# Revit family: AKTSCP38
name_source: partatom
category: Lighting Fixtures
revit_build: Autodesk Revit 2014 (Build: 20130308_1515(x64)
units: mm (PartAtom-declared; Revit-internal decimal feet)

## types (1)
- AKTSCP38
    Apparent Load = 0 VA
    Application = Commerical Indoor,Education,Healthcare,Hospitality,Office,Lobby,Conference Room,Classroom,Waiting Room,Auditorium,Guest Room,Dining Area
    Backbox = Metalic Silver
    Default Elevation = 48.000"
    Description = Stepped Cylinder track heads offer a timeless aesthetic for commercial applications such as retail, offices and hospitality
    Features = Heavy Gauge seamless construction
Regressed lamp with black baffle
Die cast swivel connection allows 110° vertical and 358° horizontal rotation
Line Voltage for up to 150W
Available in black (BL) or white (WH) baked enamel finish
    Focus Angle = 110.00°
    Lamp = 45-150W PAR38, 75-150W BR40
    Manufacturer = Prescolite
    Model = Stepped Cylinders
    Product Documentation Link = https://hubbellcdn.com
    Product Page URL = https://www.hubbell.com
    URL = https://www.hubbell.com
    Wattage Comments = 45-150W

## geometry (parser evidence)
native form markers: Blend x1, Sweep x3
no freeform markers — native parametric forms only
